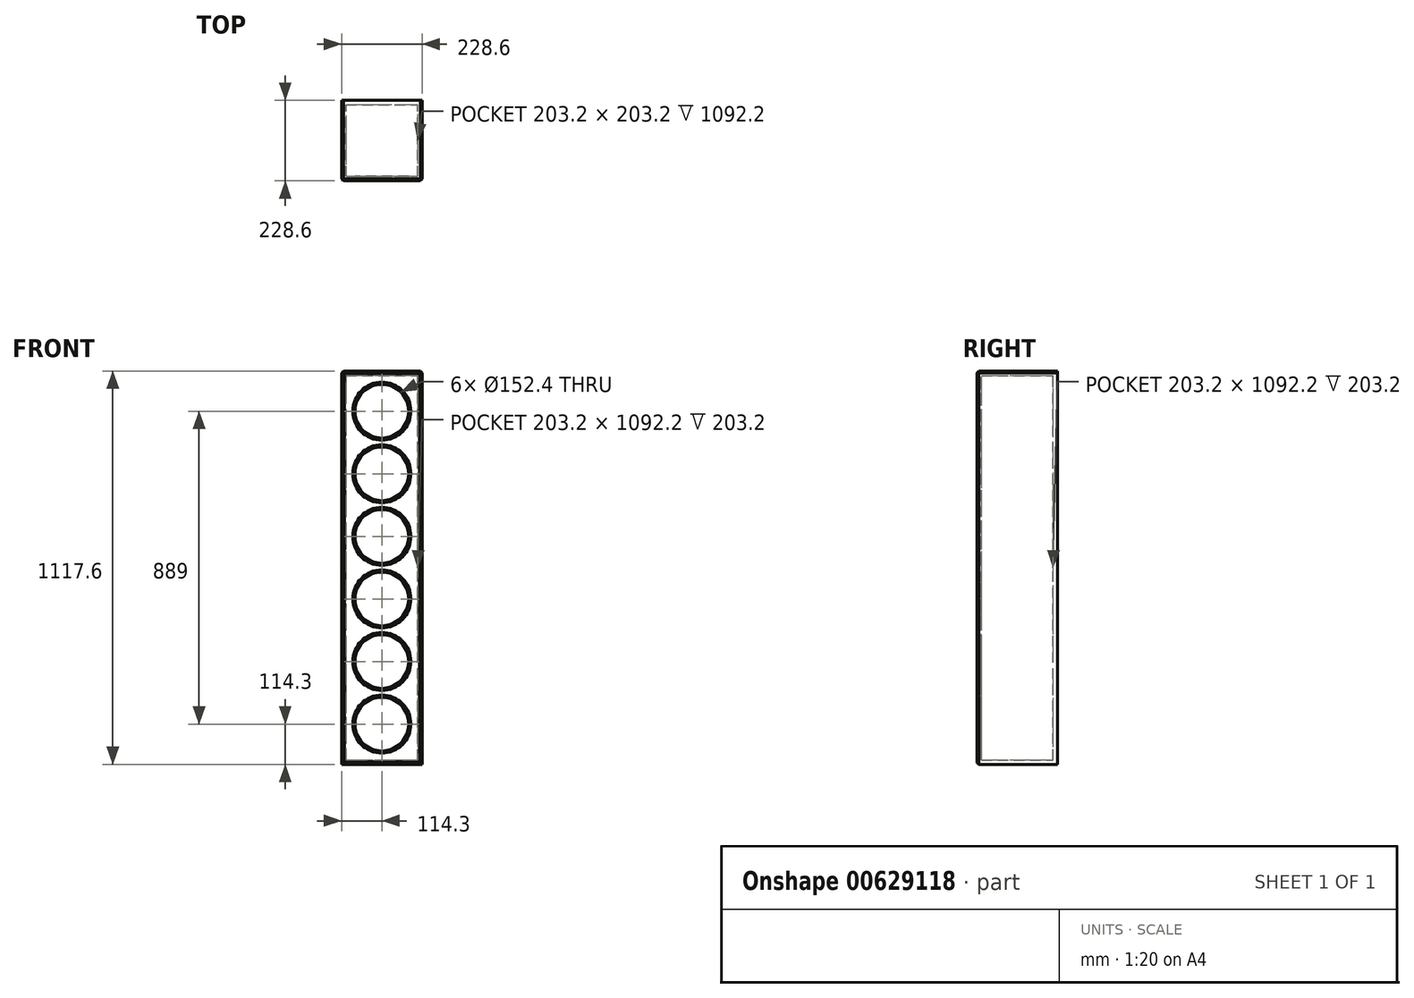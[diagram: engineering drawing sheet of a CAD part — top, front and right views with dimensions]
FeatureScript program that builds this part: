
annotation { "Feature Type Name" : "Feature", "Feature Type Description" : "" }
export const myFeature = defineFeature(function(context is Context, id is Id, definition is map)
    precondition{}
    {
        {
            var Q0;
            Q0=qCreatedBy(makeId("Front.planeOp"),FACE);
            var sketch = newSketch(context, id + "F0", { "sketchPlane" : qUnion([Q0])});
            skLineSegment(sketch, "E0.bottom", {"start": v(114.3, 558.8) * mm, "end": v(-114.3, 558.8) * mm});
            skLineSegment(sketch, "E0.top", {"start": v(114.3, -558.8) * mm, "end": v(-114.3, -558.8) * mm});
            skLineSegment(sketch, "E0.left", {"start": v(114.3, 558.8) * mm, "end": v(114.3, -558.8) * mm});
            skLineSegment(sketch, "E0.right", {"start": v(-114.3, 558.8) * mm, "end": v(-114.3, -558.8) * mm});
            skPoint(sketch, "E0.middle", {"position": v(0, 0) * mm});
            skSolve(sketch);
        }
        {
            var Q0;
            Q0 = qSketchRegion(id + "F0", true);
            extrude(context, id + "F1", {"entities" : qUnion([Q0]), "depth" : 12.7 * mm, "offsetDistance" : 25 * mm});
        }
        {
            var Q0;
            Q0=makeQuery(id+"F1.opExtrude","CAP_FACE",FACE,{"disambiguationData":[OSD([sQuery(id+"F0.wireOp",EDGE,"E0.bottom"),sQuery(id+"F0.wireOp",EDGE,"E0.top"),sQuery(id+"F0.wireOp",EDGE,"E0.left"),sQuery(id+"F0.wireOp",EDGE,"E0.right")])],"isStart":false});
            var sketch = newSketch(context, id + "F2", { "sketchPlane" : qUnion([Q0])});
            skLineSegment(sketch, "E1", {"start": v(0, 63.26) * mm, "end": v(0, 63.26) * mm});
            skLineSegment(sketch, "E2", {"start": v(-114.3, 558.8) * mm, "end": v(-114.3, -558.8) * mm});
            skLineSegment(sketch, "E3", {"start": v(-101.6, -546.1) * mm, "end": v(-101.6, 546.1) * mm});
            skLineSegment(sketch, "E4", {"start": v(-114.3, 558.8) * mm, "end": v(-101.6, 546.1) * mm});
            skLineSegment(sketch, "E5", {"start": v(-114.3, -558.8) * mm, "end": v(-101.6, -546.1) * mm});
            skLineSegment(sketch, "E6", {"start": v(-101.6, -546.1) * mm, "end": v(101.6, -546.1) * mm});
            skLineSegment(sketch, "E7", {"start": v(101.6, -546.1) * mm, "end": v(114.3, -558.8) * mm});
            skLineSegment(sketch, "E8", {"start": v(101.6, -546.1) * mm, "end": v(101.6, 546.1) * mm});
            skLineSegment(sketch, "E9", {"start": v(114.3, 558.8) * mm, "end": v(101.6, 546.1) * mm});
            skLineSegment(sketch, "E10", {"start": v(-101.6, 546.1) * mm, "end": v(101.6, 546.1) * mm});
            skSolve(sketch);
        }
        {
            var Q0;
            Q0=makeQuery(id+"F2.imprint","IMPRINT",FACE,{"disambiguationData":[TD([[makeQuery(id+"F2.imprint","IMPRINT",EDGE,{"derivedFrom":sQuery(id+"F2.wireOp",EDGE,"E2")}),1.0]])]});
            var Q1;
            Q1=makeQuery(id+"F2.imprint","IMPRINT",FACE,{"disambiguationData":[TD([[makeQuery(id+"F2.imprint","IMPRINT",EDGE,{"derivedFrom":sQuery(id+"F2.wireOp",EDGE,"E4")}),1.0]])]});
            var Q2;
            Q2=makeQuery(id+"F2.imprint","IMPRINT",FACE,{"disambiguationData":[TD([[makeQuery(id+"F2.imprint","IMPRINT",EDGE,{"derivedFrom":sQuery(id+"F2.wireOp",EDGE,"E7")}),1.0]])]});
            var Q3;
            Q3=makeQuery(id+"F2.imprint","IMPRINT",FACE,{"disambiguationData":[TD([[makeQuery(id+"F2.imprint","IMPRINT",EDGE,{"derivedFrom":sQuery(id+"F2.wireOp",EDGE,"E5")}),-1.0]])]});
            extrude(context, id + "F3", {"entities" : qUnion([Q0, Q1, Q2, Q3]), "operationType" : NewBodyOperationType.ADD, "depth" : 203.2 * mm, "offsetDistance" : 25.4 * mm});
        }
        {
            var Q0;
            Q0=makeQuery(id+"F3.opExtrude","CAP_FACE",FACE,{"disambiguationData":[OSD([sQuery(id+"F0.wireOp",EDGE,"E0.bottom"),sQuery(id+"F0.wireOp",EDGE,"E0.top"),sQuery(id+"F0.wireOp",EDGE,"E0.left"),sQuery(id+"F2.wireOp",EDGE,"E2"),sQuery(id+"F2.wireOp",EDGE,"E3"),sQuery(id+"F2.wireOp",EDGE,"E6"),sQuery(id+"F2.wireOp",EDGE,"E8"),sQuery(id+"F2.wireOp",EDGE,"E10")])],"isStart":false});
            var sketch = newSketch(context, id + "F4", { "sketchPlane" : qUnion([Q0])});
            skLineSegment(sketch, "E11.bottom", {"start": v(-114.3, 558.8) * mm, "end": v(114.3, 558.8) * mm});
            skLineSegment(sketch, "E11.top", {"start": v(-114.3, -558.8) * mm, "end": v(114.3, -558.8) * mm});
            skLineSegment(sketch, "E11.left", {"start": v(-114.3, 558.8) * mm, "end": v(-114.3, -558.8) * mm});
            skLineSegment(sketch, "E11.right", {"start": v(114.3, 558.8) * mm, "end": v(114.3, -558.8) * mm});
            skLineSegment(sketch, "E12", {"start": v(0, 558.8) * mm, "end": v(0, -558.8) * mm});
            skSolve(sketch);
        }
        {
            var Q0;
            Q0 = qSketchRegion(id + "F4", true);
            extrude(context, id + "F5", {"entities" : qUnion([Q0]), "operationType" : NewBodyOperationType.ADD, "depth" : 12.7 * mm, "offsetDistance" : 25.4 * mm});
        }
        {
            var Q0;
            Q0=makeQuery(id+"F5.opExtrude","CAP_FACE",FACE,{"disambiguationData":[OSD([sQuery(id+"F4.wireOp",EDGE,"E11.bottom"),sQuery(id+"F4.wireOp",EDGE,"E11.top"),sQuery(id+"F4.wireOp",EDGE,"E11.left"),sQuery(id+"F4.wireOp",EDGE,"E11.right")])],"isStart":false});
            var sketch = newSketch(context, id + "F6", { "sketchPlane" : qUnion([Q0])});
            skCircle(sketch, "E13", {"center": v(0, -444.5) * mm, "radius": 76.2 * mm});
            skCircle(sketch, "E14", {"center": v(0, 444.5) * mm, "radius": 76.2 * mm});
            skLineSegment(sketch, "E15", {"start": v(0, 698.14) * mm, "end": v(0, -760.9) * mm});
            skCircle(sketch, "E16", {"center": v(0, -266.7) * mm, "radius": 76.2 * mm});
            skCircle(sketch, "E17", {"center": v(0, -88.9) * mm, "radius": 76.2 * mm});
            skCircle(sketch, "E18", {"center": v(0, 88.9) * mm, "radius": 76.2 * mm});
            skCircle(sketch, "E19", {"center": v(0, 266.7) * mm, "radius": 76.2 * mm});
            skSolve(sketch);
        }
        {
            var Q0;
            Q0=sQuery(id+"F6.wireOp",VERTEX,"E13.center");
            var Q1;
            Q1=sQuery(id+"F6.wireOp",VERTEX,"E16.center");
            var Q2;
            Q2=sQuery(id+"F6.wireOp",VERTEX,"E17.center");
            var Q3;
            Q3=sQuery(id+"F6.wireOp",VERTEX,"E18.center");
            var Q4;
            Q4=sQuery(id+"F6.wireOp",VERTEX,"E19.center");
            var Q5;
            Q5=sQuery(id+"F6.wireOp",VERTEX,"E14.center");
            var Q6;
            Q6=makeQuery(id+"F1.opExtrude","SWEPT_BODY",BODY,{"disambiguationData":[OSD([sQuery(id+"F0.wireOp",EDGE,"E0.bottom"),sQuery(id+"F0.wireOp",EDGE,"E0.top"),sQuery(id+"F0.wireOp",EDGE,"E0.left"),sQuery(id+"F0.wireOp",EDGE,"E0.right")])]});
            hole(context, id + "F7", {"style" : HoleStyle.SIMPLE, "endStyle" : HoleEndStyle.BLIND, "holeDiameter" : 152.4 * mm, "majorDiameter" : 6.35 * mm, "holeDepth" : 25.4 * mm, "isTappedThrough" : true, "tappedDepth" : 12.7 * mm, "tapClearance" : 3, "locations" : qUnion([Q0, Q1, Q2, Q3, Q4, Q5]), "scope" : qUnion([Q6])});
        }
        {
            var Q0;
            Q0=makeQuery(id+"F5.opExtrude","CAP_EDGE",EDGE,{"disambiguationData":[OSD([sQuery(id+"F4.wireOp",EDGE,"E11.top")])],"isStart":false});
            var Q1;
            Q1=makeQuery(id+"F5.opExtrude","CAP_EDGE",EDGE,{"disambiguationData":[OSD([sQuery(id+"F4.wireOp",EDGE,"E11.right")])],"isStart":false});
            var Q2;
            Q2=makeQuery(id+"F5.opExtrude","CAP_EDGE",EDGE,{"disambiguationData":[OSD([sQuery(id+"F4.wireOp",EDGE,"E11.left")])],"isStart":false});
            var Q3;
            Q3=makeQuery(id+"F5.opExtrude","CAP_EDGE",EDGE,{"disambiguationData":[OSD([sQuery(id+"F4.wireOp",EDGE,"E11.bottom")])],"isStart":false});
            var Q4;
            {var subQ0=sQuery(id+"F0.wireOp",EDGE,"E0.bottom");Q4=makeQuery(id+"F5.boolean.opBoolean","MERGE",EDGE,{"derivedFrom":[makeQuery(id+"F3.boolean.opBoolean","MERGE",EDGE,{"derivedFrom":[makeQuery(id+"F1.opExtrude","SWEPT_EDGE",EDGE,{"disambiguationData":[OSD([subQ0,sQuery(id+"F0.wireOp",EDGE,"E0.right")])]}),makeQuery(id+"F3.opExtrude","SWEPT_EDGE",EDGE,{"disambiguationData":[OSD([subQ0,sQuery(id+"F2.wireOp",EDGE,"E2"),sQuery(id+"F2.wireOp",EDGE,"E4")])]})]}),makeQuery(id+"F5.opExtrude","SWEPT_EDGE",EDGE,{"disambiguationData":[OSD([sQuery(id+"F4.wireOp",EDGE,"E11.bottom"),sQuery(id+"F4.wireOp",EDGE,"E11.left")])]})]});}
            var Q5;
            {var subQ0=sQuery(id+"F0.wireOp",EDGE,"E0.left");var subQ1=sQuery(id+"F0.wireOp",EDGE,"E0.bottom");Q5=makeQuery(id+"F5.boolean.opBoolean","MERGE",EDGE,{"derivedFrom":[makeQuery(id+"F3.boolean.opBoolean","MERGE",EDGE,{"derivedFrom":[makeQuery(id+"F1.opExtrude","SWEPT_EDGE",EDGE,{"disambiguationData":[OSD([subQ1,subQ0])]}),makeQuery(id+"F3.opExtrude","SWEPT_EDGE",EDGE,{"disambiguationData":[OSD([subQ1,subQ0,sQuery(id+"F2.wireOp",EDGE,"E9")])]})]}),makeQuery(id+"F5.opExtrude","SWEPT_EDGE",EDGE,{"disambiguationData":[OSD([sQuery(id+"F4.wireOp",EDGE,"E11.bottom"),sQuery(id+"F4.wireOp",EDGE,"E11.right")])]})]});}
            chamfer(context, id + "F8", {"entities" : qUnion([Q0, Q1, Q2, Q3, Q4, Q5]), "width" : 5.08 * mm, "tangentPropagation" : true});
        }
        {
            var Q0;
            Q0=makeQuery(id+"F7.hole-0.boolean.opBoolean","COPY",EDGE,{"derivedFrom":makeQuery(id+"F7.hole-0.opRevolve","SWEPT_EDGE",EDGE,{"disambiguationData":[OSD([sQuery(id+"F7.hole-0.sketch.wireOp",EDGE,"core_line_2"),sQuery(id+"F7.hole-0.sketch.wireOp",EDGE,"core_line_3")])]})});
            var Q1;
            Q1=makeQuery(id+"F5.opExtrude","CAP_FACE",FACE,{"disambiguationData":[OSD([sQuery(id+"F4.wireOp",EDGE,"E11.bottom"),sQuery(id+"F4.wireOp",EDGE,"E11.top"),sQuery(id+"F4.wireOp",EDGE,"E11.left"),sQuery(id+"F4.wireOp",EDGE,"E11.right")])],"isStart":false});
            chamfer(context, id + "F9", {"entities" : qUnion([Q0, Q1]), "width" : 6.35 * mm});
        }
    });
